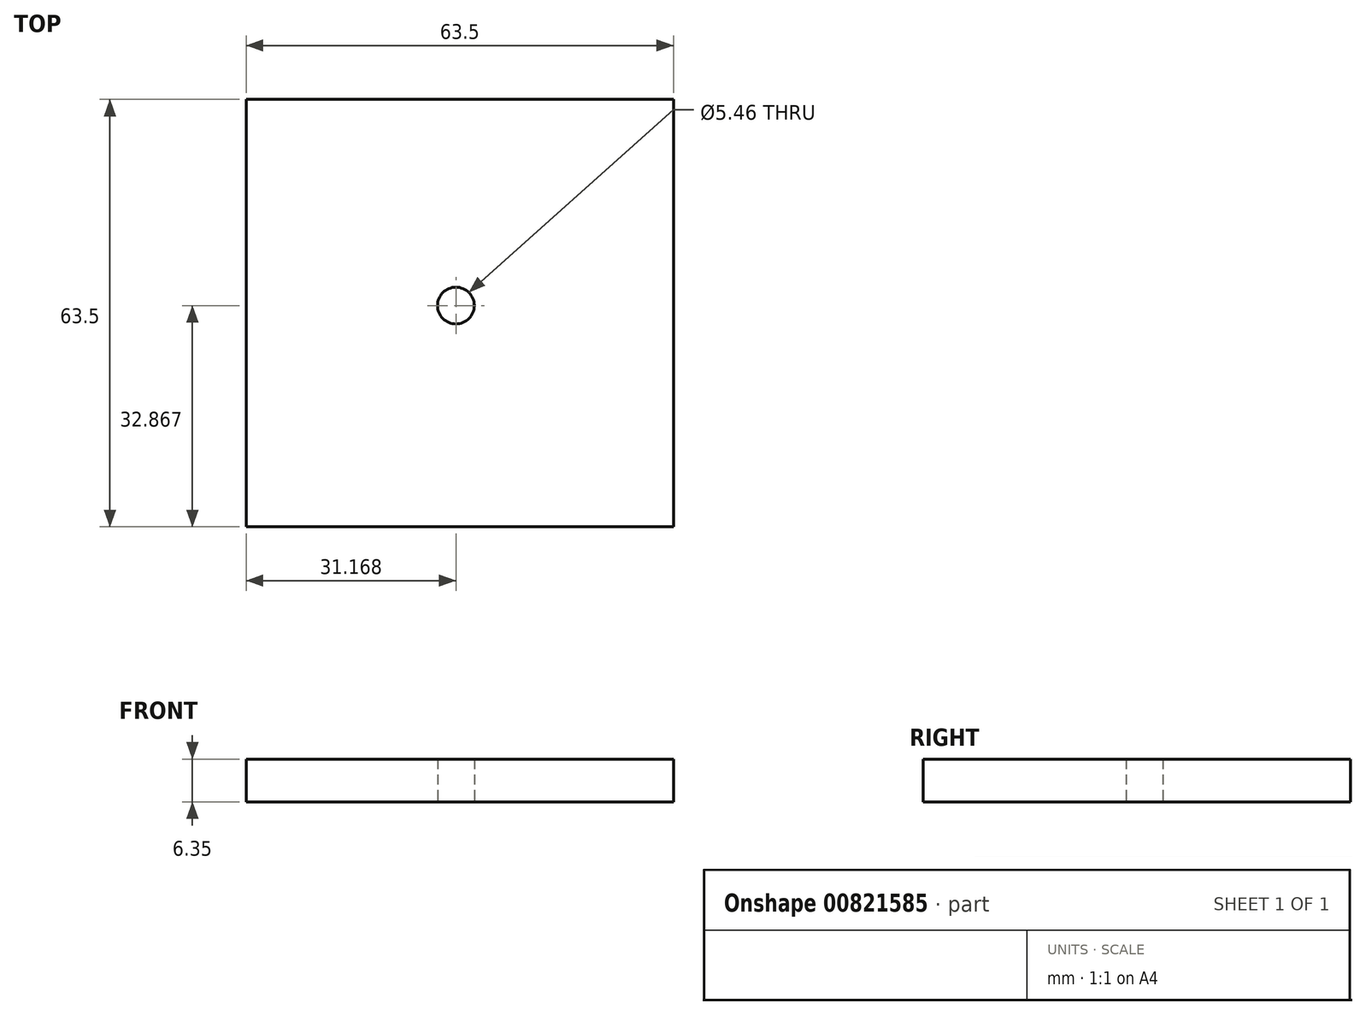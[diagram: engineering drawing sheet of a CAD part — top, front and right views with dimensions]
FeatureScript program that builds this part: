
annotation { "Feature Type Name" : "Feature", "Feature Type Description" : "" }
export const myFeature = defineFeature(function(context is Context, id is Id, definition is map)
    precondition{}
    {
        {
            var Q0;
            Q0=qCreatedBy(makeId("Top.planeOp"),FACE);
            var sketch = newSketch(context, id + "F0", { "sketchPlane" : qUnion([Q0])});
            skLineSegment(sketch, "E0.bottom", {"start": v(-33.61, 33.54) * mm, "end": v(29.89, 33.54) * mm});
            skLineSegment(sketch, "E0.top", {"start": v(-33.61, -29.96) * mm, "end": v(29.89, -29.96) * mm});
            skLineSegment(sketch, "E0.left", {"start": v(-33.61, 33.54) * mm, "end": v(-33.61, -29.96) * mm});
            skLineSegment(sketch, "E0.right", {"start": v(29.89, 33.54) * mm, "end": v(29.89, -29.96) * mm});
            skCircle(sketch, "E1", {"center": v(-2.44, 2.9) * mm, "radius": 2.73 * mm});
            skSolve(sketch);
        }
        {
            var Q0;
            Q0 = qSketchRegion(id + "F0", true);
            extrude(context, id + "F1", {"entities" : qUnion([Q0]), "depth" : 6.35 * mm, "offsetDistance" : 25.4 * mm});
        }
    });
